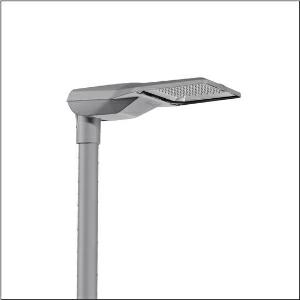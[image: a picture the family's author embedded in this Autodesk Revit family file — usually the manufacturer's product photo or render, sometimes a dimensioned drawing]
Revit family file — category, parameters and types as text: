
# Revit family: streetlight_sl_21_midi___stw1_0a_5xe7e33a08lb_1090
name_source: partatom
category: Lighting Fixtures
units: mm (PartAtom-declared; Revit-internal decimal feet)

## family parameters
Cut with Voids When Loaded = No
Host = Face
Light Source = No
Part Type = Normal
Room Calculation Point = No
Round Connector Dimension = Use Diameter
Shared = No

## types (1)
- --- (1 x LED, 14340 lm, 98.3 W, 3000K)
    Apparent Load = 98 VA
    CIE Flux Codes = 38 75 98 100 100
    Color Rendering = 70
    Color Temperature = 3000K
    Default Elevation = 1800 mm
    Description = Streetlight SL 21 midi, mast luminaire, primary light control with lens, of PMMA, primary optical cover: cover, of toughened safety glass, transparent, light distribution: STW1.0a, light emission: direct distribution, primary light characteristic: asymmetric, installation type: post-top, side-entry, LED, 3G 1.5mm², High Power LED, rated luminous flux: 14.340lm, luminous efficacy: 146lm/W, light colour: 730, colour temperature: 3000K, control: overheat protection, constant luminous flux control, time-dependent luminous flux control, flexible luminous flux parameterisation, mains connection: 220..240V, AC, 50/60Hz, connection cable pre-assembled, cable length: 10,5m, wiring characteristics: H07RN-F, start of lifetime: 98W, end of service life: 101W, reduction: 44W, luminaire housing, of diecast aluminium, powder-coated, Siteco® metallic grey (DB 702S), corrosivity category C5 mid according to DIN EN ISO 12944, please order mast flange separately, inclination adjustable: 0°, 5°, 10°, 15°, sealing non-destructively replaceable, multi-level sealing system, length: 644mm, width: 335mm, height: 110mm, mast flange for spigot size: 42mm (side-entry): 5XC10008XM4, 60/48mm (side-entry/post-top): 5XC10108XM2, 76/60mm (side-entry/post-top): 5XC10108XM1, protection rating (complete): IP66, insulation class (complete): insulation class II (safety insulation), certification: CE, ENEC, ENEC+, VDE, impact resistance: IK09, permissible operating ambient temperature for outdoor applications: -40..+50°C, standard-compliant lighting for roads and squares, packaging unit: 1 piece

Light Distribution: STW1.0a
    Height = 111 mm
    Lamp = 1 x LED
    Lamp Light Flux = 14340 lm
    Lamp Power = 98.3 W
    Lamp count = 1
    Length = 644 mm
    Luminous efficacy = 146 lm/W
    Manufacturer = Siteco
    ModVariant = No
    Model = 5XE7E33A08LB
    Number of Poles = 1
    OnlyDefault = Yes
    Power Factor = 1
    Product Name = Streetlight SL 21 midi | STW1.0a
    Product group = mast luminaire | pylon top
    ProductGroupID = 6100
    Protection Class = Protection class II
    Protection Degree = IP 66
    RLX_Detail_Level = 1
    RLX_Emergency_Light_Flux = 0 lm
    RLX_Emergency_Type = 0
    RLX_Emergency_Type_DB = No
    RlxData = <blob elided: 90565 chars, md5=ac17e7e8>
    Socket = socket
    Standby Power = 0 W
    System Light Flux = 14340 lm
    System Power = 98 W
    Type Comments = factory setting: luminous flux: 100 % | Output Level: 100 % | 1020 mA
    Type Image = l_1004298.jpg
    URL = http://relux.com
    VarID = @adj_121289
    Voltage = 0 V
    Weight = 0.00 kg
    Width = 336 mm

## geometry (parser evidence)
native form markers: Blend x4, Sweep x12
no freeform markers — native parametric forms only
